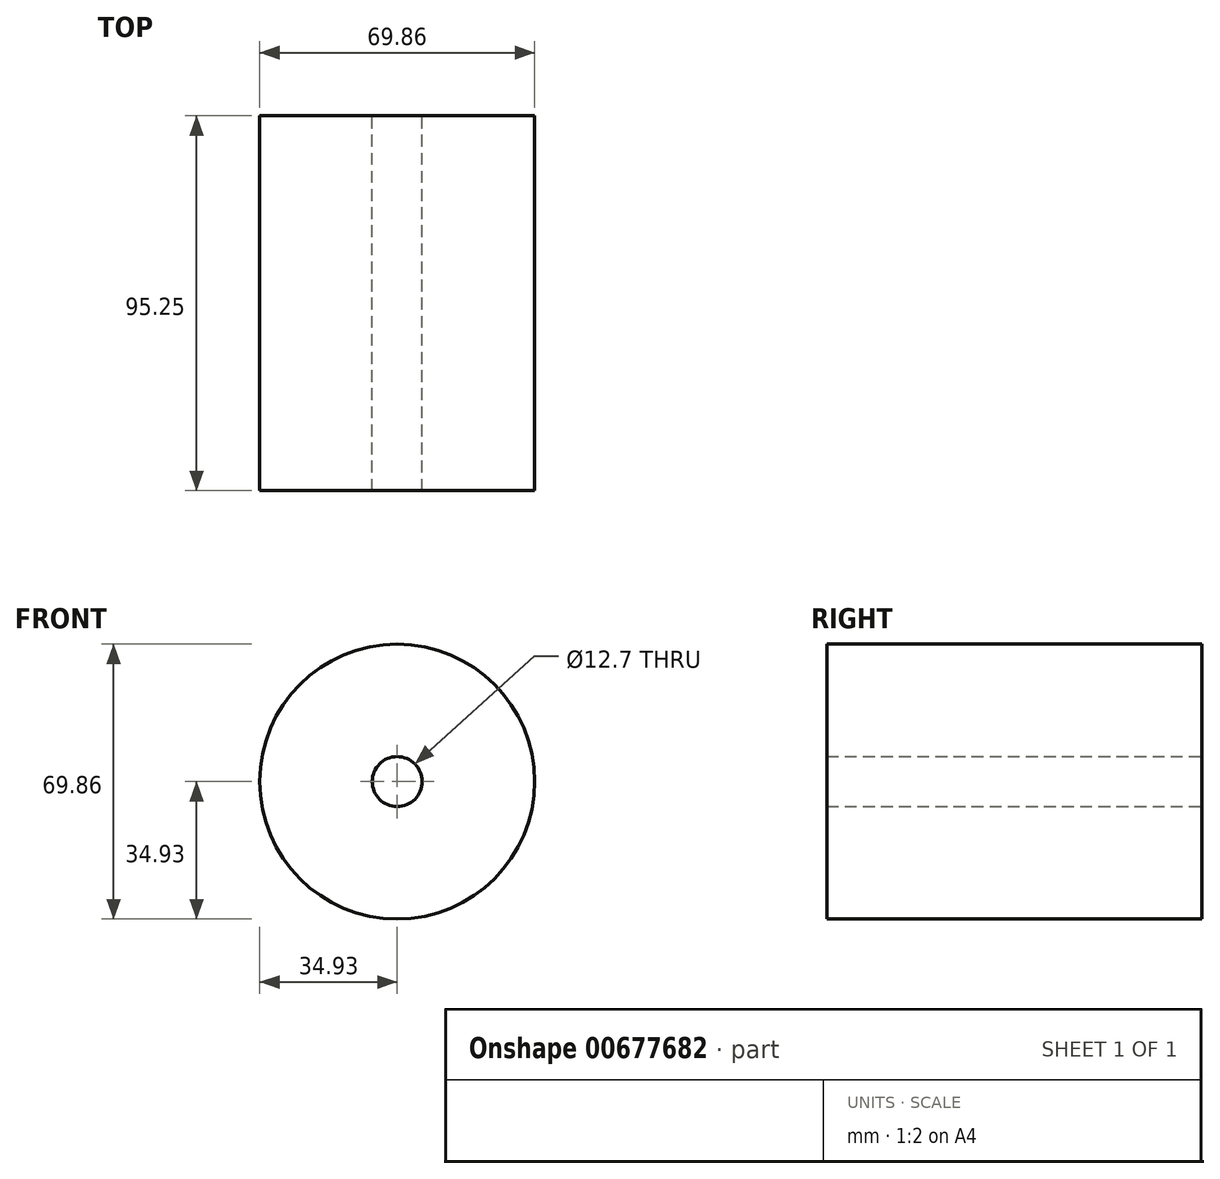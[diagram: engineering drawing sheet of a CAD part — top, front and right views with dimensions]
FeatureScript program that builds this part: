
annotation { "Feature Type Name" : "Feature", "Feature Type Description" : "" }
export const myFeature = defineFeature(function(context is Context, id is Id, definition is map)
    precondition{}
    {
        {
            var Q0;
            Q0=qCreatedBy(makeId("Front.planeOp"),FACE);
            var sketch = newSketch(context, id + "F0", { "sketchPlane" : qUnion([Q0])});
            skCircle(sketch, "E0", {"center": v(0, 0) * mm, "radius": 34.93 * mm});
            skCircle(sketch, "E1", {"center": v(0, 0) * mm, "radius": 6.35 * mm});
            skSolve(sketch);
        }
        {
            var Q0;
            Q0=makeQuery(id+"F0.imprint","IMPRINT",FACE,{"disambiguationData":[TD([[makeQuery(id+"F0.imprint","IMPRINT",EDGE,{"derivedFrom":sQuery(id+"F0.wireOp",EDGE,"E0")}),1.0]])]});
            extrude(context, id + "F1", {"entities" : qUnion([Q0]), "depth" : 95.25 * mm, "offsetDistance" : 25.4 * mm});
        }
    });
